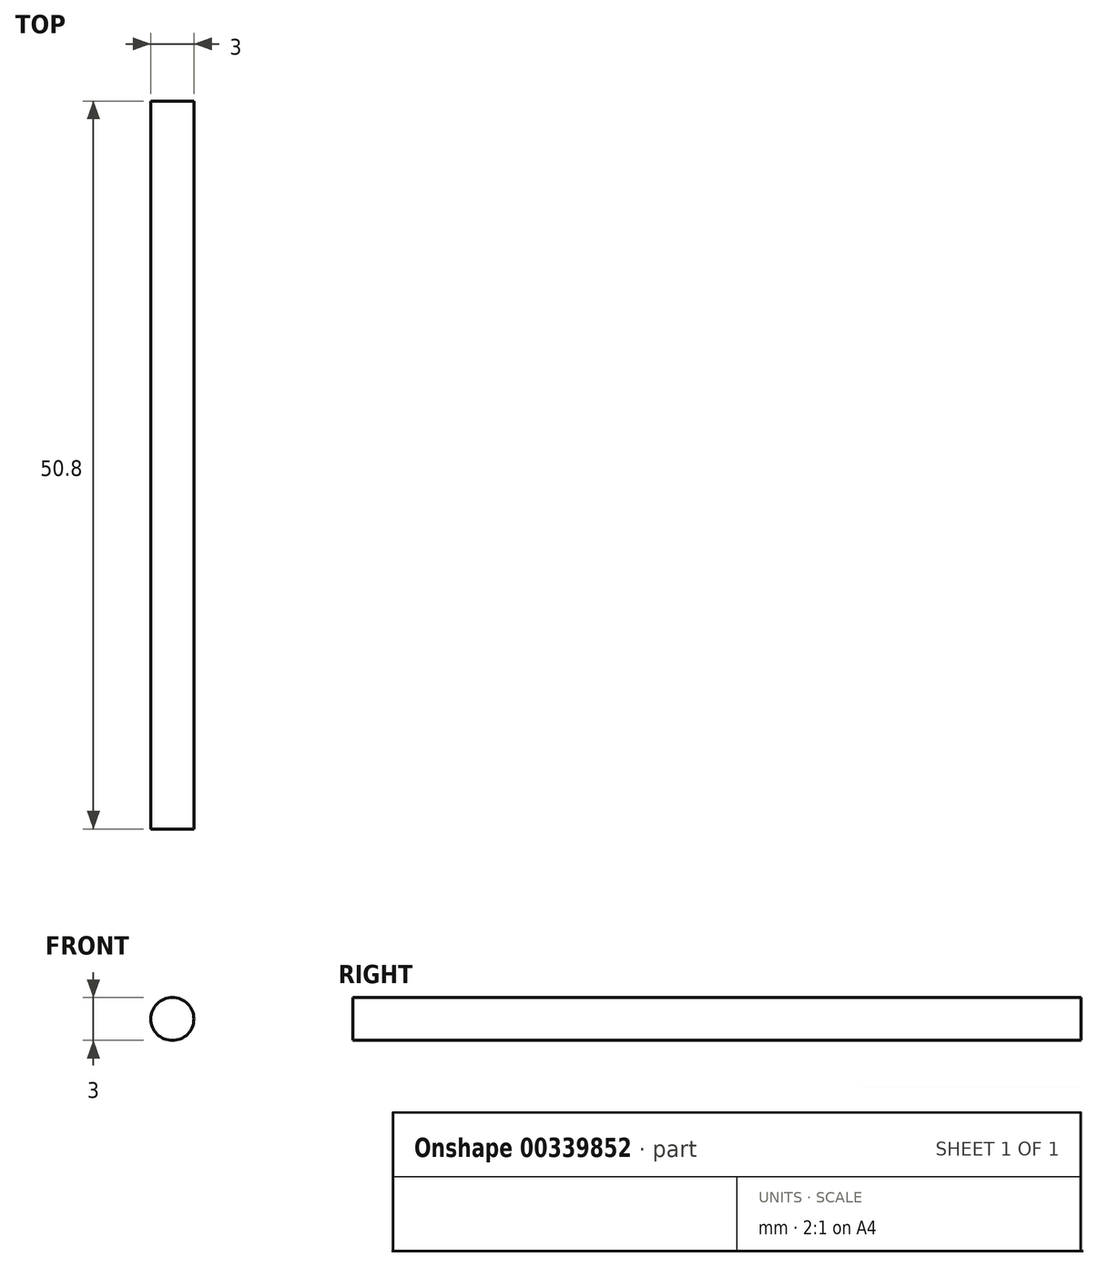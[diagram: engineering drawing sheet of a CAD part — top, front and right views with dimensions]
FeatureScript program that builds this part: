
annotation { "Feature Type Name" : "Feature", "Feature Type Description" : "" }
export const myFeature = defineFeature(function(context is Context, id is Id, definition is map)
    precondition{}
    {
        {
            var Q0;
            Q0=qCreatedBy(makeId("Front.planeOp"),FACE);
            var sketch = newSketch(context, id + "F0", { "sketchPlane" : qUnion([Q0])});
            skCircle(sketch, "E0", {"center": v(-32.96, 25.49) * mm, "radius": 1.5 * mm});
            skSolve(sketch);
        }
        {
            var Q0;
            Q0=makeQuery(id+"F0.imprint","IMPRINT",FACE,{"disambiguationData":[TD([[makeQuery(id+"F0.imprint","IMPRINT",EDGE,{"derivedFrom":sQuery(id+"F0.wireOp",EDGE,"E0")}),1.0]])]});
            extrude(context, id + "F1", {"entities" : qUnion([Q0]), "depth" : 50.8 * mm});
        }
    });
